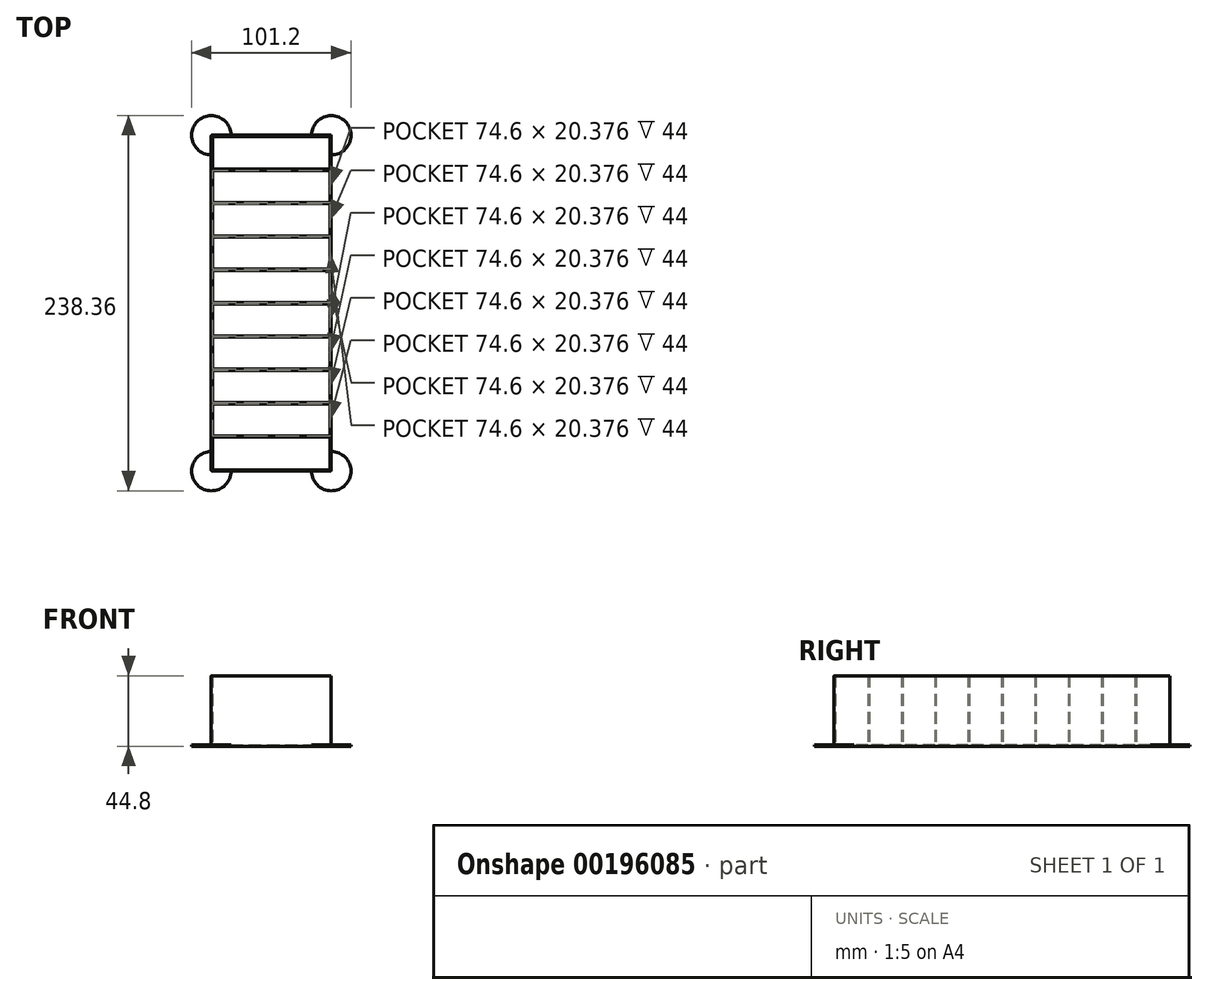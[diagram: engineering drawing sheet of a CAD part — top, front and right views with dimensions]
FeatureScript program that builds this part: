
annotation { "Feature Type Name" : "Feature", "Feature Type Description" : "" }
export const myFeature = defineFeature(function(context is Context, id is Id, definition is map)
    precondition{}
    {
        {
            var Q0;
            Q0=qCreatedBy(makeId("Top.planeOp"),FACE);
            var sketch = newSketch(context, id + "F0", { "sketchPlane" : qUnion([Q0])});
            skLineSegment(sketch, "E0.bottom", {"start": v(0, 0) * mm, "end": v(76.2, 0) * mm});
            skLineSegment(sketch, "E0.top", {"start": v(0, 213.36) * mm, "end": v(76.2, 213.36) * mm});
            skLineSegment(sketch, "E0.left", {"start": v(0, 0) * mm, "end": v(0, 213.36) * mm});
            skLineSegment(sketch, "E0.right", {"start": v(76.2, 0) * mm, "end": v(76.2, 213.36) * mm});
            skCircle(sketch, "E1", {"center": v(76.2, 0) * mm, "radius": 12.5 * mm});
            skCircle(sketch, "E2", {"center": v(0, 0) * mm, "radius": 12.5 * mm});
            skCircle(sketch, "E3", {"center": v(76.2, 213.36) * mm, "radius": 12.5 * mm});
            skCircle(sketch, "E4", {"center": v(0, 213.36) * mm, "radius": 12.5 * mm});
            skSolve(sketch);
        }
        {
            var Q0;
            Q0=makeQuery(id+"F0.imprint","IMPRINT",FACE,{"disambiguationData":[TD([[makeQuery(id+"F0.imprint","IMPRINT",EDGE,{"derivedFrom":sQuery(id+"F0.wireOp",EDGE,"E0.bottom")}),1.0]])]});
            var Q1;
            {var subQ5=sQuery(id+"F0.wireOp",EDGE,"E2");var subQ10=sQuery(id+"F0.wireOp",EDGE,"E0.bottom");var subQ11=makeQuery(id+"F0.imprint","INTERSECT",VERTEX,{"derivedFrom":[subQ10,subQ5]});Q1=makeQuery(id+"F0.imprint","IMPRINT",FACE,{"disambiguationData":[TD([[makeQuery(id+"F0.imprint","IMPRINT",EDGE,{"disambiguationData":[TD([[subQ11,-1.0]])],"derivedFrom":subQ10}),1.0]])]});}
            var Q2;
            {var subQ0=sQuery(id+"F0.wireOp",EDGE,"E0.right");var subQ1=sQuery(id+"F0.wireOp",EDGE,"E0.top");var subQ2=makeQuery(id+"F0.imprint","INTERSECT",VERTEX,{"derivedFrom":[subQ1,subQ0]});Q2=makeQuery(id+"F0.imprint","IMPRINT",FACE,{"disambiguationData":[TD([[makeQuery(id+"F0.imprint","IMPRINT",EDGE,{"disambiguationData":[TD([[subQ2,1.0]])],"derivedFrom":subQ1}),-1.0]])]});}
            var Q3;
            {var subQ0=sQuery(id+"F0.wireOp",EDGE,"E0.left");var subQ1=sQuery(id+"F0.wireOp",EDGE,"E0.top");var subQ2=makeQuery(id+"F0.imprint","INTERSECT",VERTEX,{"derivedFrom":[subQ1,subQ0]});Q3=makeQuery(id+"F0.imprint","IMPRINT",FACE,{"disambiguationData":[TD([[makeQuery(id+"F0.imprint","IMPRINT",EDGE,{"disambiguationData":[TD([[subQ2,-1.0]])],"derivedFrom":subQ1}),-1.0]])]});}
            extrude(context, id + "F1", {"entities" : qUnion([Q0, Q1, Q2, Q3]), "depth" : 0.8 * mm});
        }
        {
            var Q0;
            Q0=makeQuery(id+"F1.opExtrude","CAP_FACE",FACE,{"disambiguationData":[OSD([sQuery(id+"F0.wireOp",EDGE,"E0.bottom"),sQuery(id+"F0.wireOp",EDGE,"E0.top"),sQuery(id+"F0.wireOp",EDGE,"E0.left"),sQuery(id+"F0.wireOp",EDGE,"E0.right")])],"isStart":false});
            var sketch = newSketch(context, id + "F2", { "sketchPlane" : qUnion([Q0])});
            skLineSegment(sketch, "E5.0", {"start": v(0, 0) * mm, "end": v(0, 213.36) * mm});
            skLineSegment(sketch, "E5.1", {"start": v(0, 213.36) * mm, "end": v(76.2, 213.36) * mm});
            skLineSegment(sketch, "E5.2", {"start": v(76.2, 0) * mm, "end": v(76.2, 213.36) * mm});
            skLineSegment(sketch, "E5.3", {"start": v(0, 0) * mm, "end": v(76.2, 0) * mm});
            skLineSegment(sketch, "E6.bottom", {"start": v(0.8, 212.56) * mm, "end": v(75.4, 212.56) * mm});
            skLineSegment(sketch, "E6.top", {"start": v(0.8, 0.8) * mm, "end": v(75.4, 0.8) * mm});
            skLineSegment(sketch, "E6.left", {"start": v(0.8, 212.56) * mm, "end": v(0.8, 191.78) * mm});
            skLineSegment(sketch, "E6.right", {"start": v(75.4, 212.56) * mm, "end": v(75.4, 191.78) * mm});
            skLineSegment(sketch, "E7.0.1.0", {"start": v(0.8, 191.38) * mm, "end": v(75.4, 191.38) * mm, "construction": true});
            skLineSegment(sketch, "E7.0.2.0", {"start": v(0.8, 170.2) * mm, "end": v(75.4, 170.2) * mm, "construction": true});
            skLineSegment(sketch, "E7.0.3.0", {"start": v(0.8, 149.03) * mm, "end": v(75.4, 149.03) * mm, "construction": true});
            skLineSegment(sketch, "E7.0.4.0", {"start": v(0.8, 127.86) * mm, "end": v(75.4, 127.86) * mm, "construction": true});
            skLineSegment(sketch, "E7.0.5.0", {"start": v(0.8, 106.68) * mm, "end": v(75.4, 106.68) * mm, "construction": true});
            skLineSegment(sketch, "E7.0.6.0", {"start": v(0.8, 85.5) * mm, "end": v(75.4, 85.5) * mm, "construction": true});
            skLineSegment(sketch, "E7.0.7.0", {"start": v(0.8, 64.33) * mm, "end": v(75.4, 64.33) * mm, "construction": true});
            skLineSegment(sketch, "E7.0.8.0", {"start": v(0.8, 43.15) * mm, "end": v(75.4, 43.15) * mm, "construction": true});
            skLineSegment(sketch, "E7.0.9.0", {"start": v(0.8, 21.98) * mm, "end": v(75.4, 21.98) * mm, "construction": true});
            skLineSegment(sketch, "E7.direction1", {"start": v(0.8, 212.56) * mm, "end": v(25.8, 212.56) * mm, "construction": true});
            skLineSegment(sketch, "E7.direction2", {"start": v(0.8, 212.56) * mm, "end": v(0.8, 191.78) * mm, "construction": true});
            skLineSegment(sketch, "E8", {"start": v(0.8, 191.78) * mm, "end": v(75.4, 191.78) * mm});
            skLineSegment(sketch, "E9", {"start": v(75.4, 190.98) * mm, "end": v(0.8, 190.98) * mm});
            skLineSegment(sketch, "E10.trimOffspring", {"start": v(75.4, 190.98) * mm, "end": v(75.4, 170.6) * mm});
            skLineSegment(sketch, "E11.trimOffspring", {"start": v(0.8, 190.98) * mm, "end": v(0.8, 170.6) * mm});
            skLineSegment(sketch, "E12.0.0.10", {"start": v(0.8, 0.8) * mm, "end": v(75.4, 0.8) * mm, "construction": true});
            skLineSegment(sketch, "E13", {"start": v(0.8, 170.6) * mm, "end": v(75.4, 170.6) * mm});
            skLineSegment(sketch, "E14", {"start": v(75.4, 169.8) * mm, "end": v(0.8, 169.8) * mm});
            skLineSegment(sketch, "E15.trimOffspring", {"start": v(75.4, 169.8) * mm, "end": v(75.4, 149.43) * mm});
            skLineSegment(sketch, "E16.trimOffspring", {"start": v(0.8, 169.8) * mm, "end": v(0.8, 149.43) * mm});
            skLineSegment(sketch, "E17", {"start": v(0.8, 149.43) * mm, "end": v(75.4, 149.43) * mm});
            skLineSegment(sketch, "E18", {"start": v(0.8, 148.63) * mm, "end": v(75.4, 148.63) * mm});
            skLineSegment(sketch, "E19.trimOffspring", {"start": v(75.4, 148.63) * mm, "end": v(75.4, 128.26) * mm});
            skLineSegment(sketch, "E20.trimOffspring", {"start": v(0.8, 148.63) * mm, "end": v(0.8, 128.26) * mm});
            skLineSegment(sketch, "E21", {"start": v(0.8, 128.26) * mm, "end": v(75.4, 128.26) * mm});
            skLineSegment(sketch, "E22", {"start": v(0.8, 127.46) * mm, "end": v(75.4, 127.46) * mm});
            skLineSegment(sketch, "E23.trimOffspring", {"start": v(75.4, 127.46) * mm, "end": v(75.4, 107.08) * mm});
            skLineSegment(sketch, "E24.trimOffspring", {"start": v(0.8, 127.46) * mm, "end": v(0.8, 107.08) * mm});
            skLineSegment(sketch, "E25", {"start": v(0.8, 107.08) * mm, "end": v(75.4, 107.08) * mm});
            skLineSegment(sketch, "E26", {"start": v(75.4, 106.28) * mm, "end": v(0.8, 106.28) * mm});
            skLineSegment(sketch, "E27", {"start": v(0.8, 85.9) * mm, "end": v(75.4, 85.9) * mm});
            skLineSegment(sketch, "E28", {"start": v(75.4, 85.1) * mm, "end": v(0.8, 85.1) * mm});
            skLineSegment(sketch, "E29", {"start": v(0.8, 64.73) * mm, "end": v(75.4, 64.73) * mm});
            skLineSegment(sketch, "E30", {"start": v(75.4, 63.93) * mm, "end": v(0.8, 63.93) * mm});
            skLineSegment(sketch, "E31", {"start": v(0.8, 43.55) * mm, "end": v(75.4, 43.55) * mm});
            skLineSegment(sketch, "E32", {"start": v(75.4, 42.75) * mm, "end": v(0.8, 42.75) * mm});
            skLineSegment(sketch, "E33", {"start": v(0.8, 22.38) * mm, "end": v(75.4, 22.38) * mm});
            skLineSegment(sketch, "E34", {"start": v(75.4, 21.58) * mm, "end": v(0.8, 21.58) * mm});
            skLineSegment(sketch, "E35.trimOffspring", {"start": v(75.4, 106.28) * mm, "end": v(75.4, 85.9) * mm});
            skLineSegment(sketch, "E36.trimOffspring", {"start": v(75.4, 85.1) * mm, "end": v(75.4, 64.73) * mm});
            skLineSegment(sketch, "E37.trimOffspring", {"start": v(75.4, 63.93) * mm, "end": v(75.4, 43.55) * mm});
            skLineSegment(sketch, "E38.trimOffspring", {"start": v(75.4, 42.75) * mm, "end": v(75.4, 22.38) * mm});
            skLineSegment(sketch, "E39.trimOffspring", {"start": v(75.4, 21.58) * mm, "end": v(75.4, 0.8) * mm});
            skLineSegment(sketch, "E40.trimOffspring", {"start": v(0.8, 21.58) * mm, "end": v(0.8, 0.8) * mm});
            skLineSegment(sketch, "E41.trimOffspring", {"start": v(0.8, 42.75) * mm, "end": v(0.8, 22.38) * mm});
            skLineSegment(sketch, "E42.trimOffspring", {"start": v(0.8, 63.93) * mm, "end": v(0.8, 43.55) * mm});
            skLineSegment(sketch, "E43.trimOffspring", {"start": v(0.8, 85.1) * mm, "end": v(0.8, 64.73) * mm});
            skLineSegment(sketch, "E44.trimOffspring", {"start": v(0.8, 106.28) * mm, "end": v(0.8, 85.9) * mm});
            skSolve(sketch);
        }
        {
            var Q0;
            Q0=makeQuery(id+"F2.imprint","IMPRINT",FACE,{"disambiguationData":[TD([[makeQuery(id+"F2.imprint","IMPRINT",EDGE,{"derivedFrom":sQuery(id+"F2.wireOp",EDGE,"E5.0")}),-1.0]])]});
            extrude(context, id + "F3", {"entities" : qUnion([Q0]), "operationType" : NewBodyOperationType.ADD, "depth" : 44 * mm});
        }
        {
            var Q0;
            Q0=makeQuery(id+"F3.opExtrude","SWEPT_EDGE",EDGE,{"disambiguationData":[OSD([sQuery(id+"F2.wireOp",EDGE,"E6.top"),sQuery(id+"F2.wireOp",EDGE,"E39.trimOffspring")])]});
            var Q1;
            Q1=makeQuery(id+"F3.boolean.opBoolean","MERGE",EDGE,{"derivedFrom":[makeQuery(id+"F1.opExtrude","SWEPT_EDGE",EDGE,{"disambiguationData":[OSD([sQuery(id+"F0.wireOp",EDGE,"E0.bottom"),sQuery(id+"F0.wireOp",EDGE,"E0.right")])]}),makeQuery(id+"F3.opExtrude","SWEPT_EDGE",EDGE,{"disambiguationData":[OSD([sQuery(id+"F2.wireOp",EDGE,"E5.2"),sQuery(id+"F2.wireOp",EDGE,"E5.3")])]})]});
            var Q2;
            Q2=makeQuery(id+"F3.opExtrude","SWEPT_EDGE",EDGE,{"disambiguationData":[OSD([sQuery(id+"F2.wireOp",EDGE,"E6.top"),sQuery(id+"F2.wireOp",EDGE,"E40.trimOffspring")])]});
            var Q3;
            Q3=makeQuery(id+"F3.boolean.opBoolean","MERGE",EDGE,{"derivedFrom":[makeQuery(id+"F1.opExtrude","SWEPT_EDGE",EDGE,{"disambiguationData":[OSD([sQuery(id+"F0.wireOp",EDGE,"E0.bottom"),sQuery(id+"F0.wireOp",EDGE,"E0.left")])]}),makeQuery(id+"F3.opExtrude","SWEPT_EDGE",EDGE,{"disambiguationData":[OSD([sQuery(id+"F2.wireOp",EDGE,"E5.0"),sQuery(id+"F2.wireOp",EDGE,"E5.3")])]})]});
            var Q4;
            Q4=makeQuery(id+"F3.boolean.opBoolean","MERGE",EDGE,{"derivedFrom":[makeQuery(id+"F1.opExtrude","SWEPT_EDGE",EDGE,{"disambiguationData":[OSD([sQuery(id+"F0.wireOp",EDGE,"E0.top"),sQuery(id+"F0.wireOp",EDGE,"E0.left")])]}),makeQuery(id+"F3.opExtrude","SWEPT_EDGE",EDGE,{"disambiguationData":[OSD([sQuery(id+"F2.wireOp",EDGE,"E5.0"),sQuery(id+"F2.wireOp",EDGE,"E5.1")])]})]});
            var Q5;
            Q5=makeQuery(id+"F3.opExtrude","SWEPT_EDGE",EDGE,{"disambiguationData":[OSD([sQuery(id+"F2.wireOp",EDGE,"E6.bottom"),sQuery(id+"F2.wireOp",EDGE,"E6.left")])]});
            var Q6;
            Q6=makeQuery(id+"F3.boolean.opBoolean","MERGE",EDGE,{"derivedFrom":[makeQuery(id+"F1.opExtrude","SWEPT_EDGE",EDGE,{"disambiguationData":[OSD([sQuery(id+"F0.wireOp",EDGE,"E0.top"),sQuery(id+"F0.wireOp",EDGE,"E0.right")])]}),makeQuery(id+"F3.opExtrude","SWEPT_EDGE",EDGE,{"disambiguationData":[OSD([sQuery(id+"F2.wireOp",EDGE,"E5.1"),sQuery(id+"F2.wireOp",EDGE,"E5.2")])]})]});
            var Q7;
            Q7=makeQuery(id+"F3.opExtrude","SWEPT_EDGE",EDGE,{"disambiguationData":[OSD([sQuery(id+"F2.wireOp",EDGE,"E6.bottom"),sQuery(id+"F2.wireOp",EDGE,"E6.right")])]});
            fillet(context, id + "F4", {"entities" : qUnion([Q0, Q1, Q2, Q3, Q4, Q5, Q6, Q7]), "radius" : 0.4 * mm, "tangentPropagation" : true, "allowEdgeOverflow" : false});
        }
        {
            var Q0;
            {var subQ0=sQuery(id+"F0.wireOp",EDGE,"E0.right");var subQ1=sQuery(id+"F0.wireOp",EDGE,"E0.bottom");var subQ2=makeQuery(id+"F0.imprint","INTERSECT",VERTEX,{"derivedFrom":[subQ1,subQ0]});Q0=makeQuery(id+"F0.imprint","IMPRINT",FACE,{"disambiguationData":[TD([[makeQuery(id+"F0.imprint","IMPRINT",EDGE,{"disambiguationData":[TD([[subQ2,1.0]])],"derivedFrom":subQ1}),-1.0]])]});}
            var Q1;
            {var subQ0=sQuery(id+"F0.wireOp",EDGE,"E0.left");var subQ1=sQuery(id+"F0.wireOp",EDGE,"E0.bottom");var subQ2=makeQuery(id+"F0.imprint","INTERSECT",VERTEX,{"derivedFrom":[subQ1,subQ0]});Q1=makeQuery(id+"F0.imprint","IMPRINT",FACE,{"disambiguationData":[TD([[makeQuery(id+"F0.imprint","IMPRINT",EDGE,{"disambiguationData":[TD([[subQ2,-1.0]])],"derivedFrom":subQ1}),-1.0]])]});}
            var Q2;
            {var subQ0=sQuery(id+"F0.wireOp",EDGE,"E0.left");var subQ1=sQuery(id+"F0.wireOp",EDGE,"E0.top");var subQ2=makeQuery(id+"F0.imprint","INTERSECT",VERTEX,{"derivedFrom":[subQ1,subQ0]});Q2=makeQuery(id+"F0.imprint","IMPRINT",FACE,{"disambiguationData":[TD([[makeQuery(id+"F0.imprint","IMPRINT",EDGE,{"disambiguationData":[TD([[subQ2,-1.0]])],"derivedFrom":subQ1}),1.0]])]});}
            var Q3;
            {var subQ0=sQuery(id+"F0.wireOp",EDGE,"E0.right");var subQ1=sQuery(id+"F0.wireOp",EDGE,"E0.top");var subQ2=makeQuery(id+"F0.imprint","INTERSECT",VERTEX,{"derivedFrom":[subQ1,subQ0]});Q3=makeQuery(id+"F0.imprint","IMPRINT",FACE,{"disambiguationData":[TD([[makeQuery(id+"F0.imprint","IMPRINT",EDGE,{"disambiguationData":[TD([[subQ2,1.0]])],"derivedFrom":subQ1}),1.0]])]});}
            var Q4;
            {var subQ0=sQuery(id+"F0.wireOp",EDGE,"E0.right");var subQ1=sQuery(id+"F0.wireOp",EDGE,"E0.bottom");var subQ2=makeQuery(id+"F0.imprint","INTERSECT",VERTEX,{"derivedFrom":[subQ1,subQ0]});Q4=makeQuery(id+"F0.imprint","IMPRINT",FACE,{"disambiguationData":[TD([[makeQuery(id+"F0.imprint","IMPRINT",EDGE,{"disambiguationData":[TD([[subQ2,1.0]])],"derivedFrom":subQ1}),1.0]])]});}
            var Q5;
            {var subQ0=sQuery(id+"F0.wireOp",EDGE,"E0.left");var subQ1=sQuery(id+"F0.wireOp",EDGE,"E0.bottom");var subQ2=makeQuery(id+"F0.imprint","INTERSECT",VERTEX,{"derivedFrom":[subQ1,subQ0]});Q5=makeQuery(id+"F0.imprint","IMPRINT",FACE,{"disambiguationData":[TD([[makeQuery(id+"F0.imprint","IMPRINT",EDGE,{"disambiguationData":[TD([[subQ2,-1.0]])],"derivedFrom":subQ1}),1.0]])]});}
            var Q6;
            {var subQ0=sQuery(id+"F0.wireOp",EDGE,"E0.left");var subQ1=sQuery(id+"F0.wireOp",EDGE,"E0.top");var subQ2=makeQuery(id+"F0.imprint","INTERSECT",VERTEX,{"derivedFrom":[subQ1,subQ0]});Q6=makeQuery(id+"F0.imprint","IMPRINT",FACE,{"disambiguationData":[TD([[makeQuery(id+"F0.imprint","IMPRINT",EDGE,{"disambiguationData":[TD([[subQ2,-1.0]])],"derivedFrom":subQ1}),-1.0]])]});}
            var Q7;
            {var subQ0=sQuery(id+"F0.wireOp",EDGE,"E0.right");var subQ1=sQuery(id+"F0.wireOp",EDGE,"E0.top");var subQ2=makeQuery(id+"F0.imprint","INTERSECT",VERTEX,{"derivedFrom":[subQ1,subQ0]});Q7=makeQuery(id+"F0.imprint","IMPRINT",FACE,{"disambiguationData":[TD([[makeQuery(id+"F0.imprint","IMPRINT",EDGE,{"disambiguationData":[TD([[subQ2,1.0]])],"derivedFrom":subQ1}),-1.0]])]});}
            var Q8;
            Q8=makeQuery(id+"F3.boolean.opBoolean","SPLIT",FACE,{"disambiguationData":[TD([makeQuery(id+"F3.opExtrude","SWEPT_FACE",FACE,{"disambiguationData":[OSD([sQuery(id+"F2.wireOp",EDGE,"E6.top")])]})])],"derivedFrom":makeQuery(id+"F1.opExtrude","CAP_FACE",FACE,{"disambiguationData":[OSD([sQuery(id+"F0.wireOp",EDGE,"E0.bottom"),sQuery(id+"F0.wireOp",EDGE,"E0.top"),sQuery(id+"F0.wireOp",EDGE,"E0.left"),sQuery(id+"F0.wireOp",EDGE,"E0.right")])],"isStart":false})});
            extrude(context, id + "F5", {"entities" : qUnion([Q0, Q1, Q2, Q3, Q4, Q5, Q6, Q7]), "operationType" : NewBodyOperationType.ADD, "endBound" : BoundingType.UP_TO_SURFACE, "endBoundEntityFace" : qUnion([Q8]), "depth" : 25 * mm});
        }
    });
